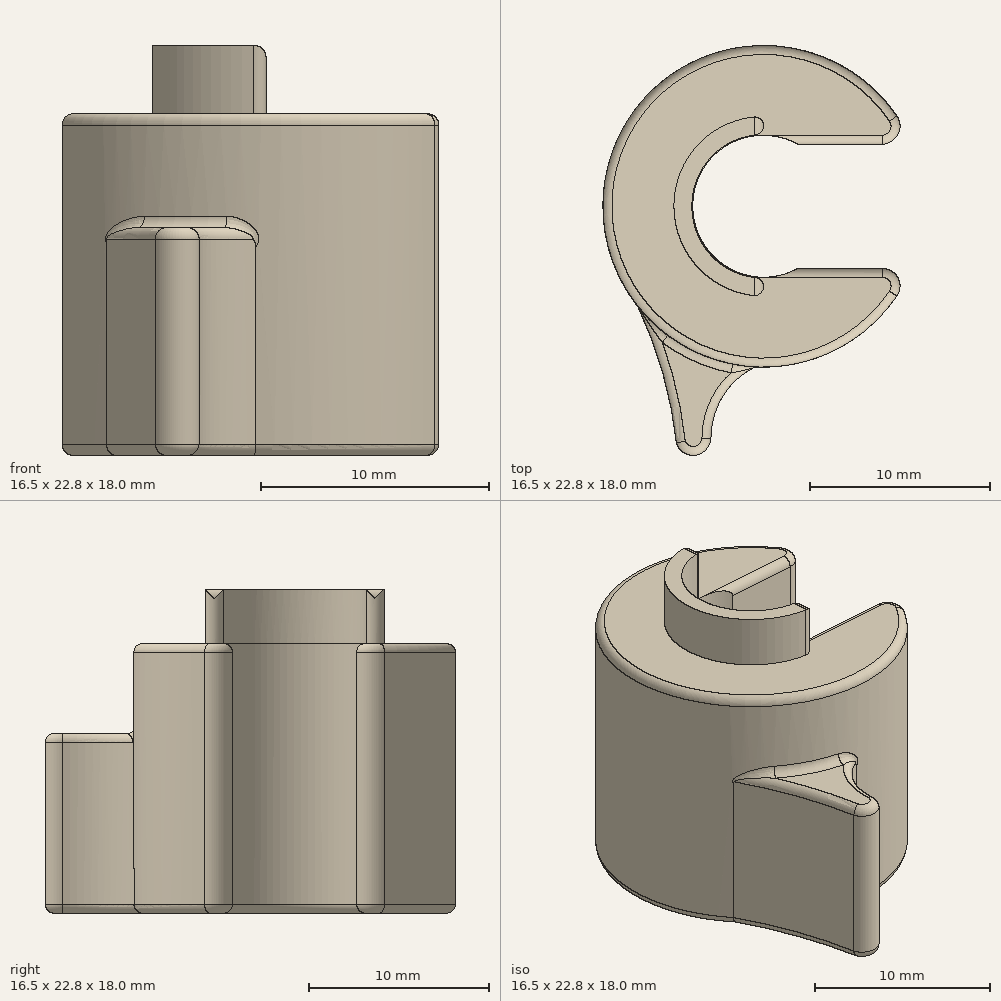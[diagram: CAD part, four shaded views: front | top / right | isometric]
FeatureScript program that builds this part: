
annotation { "Feature Type Name" : "Feature", "Feature Type Description" : "" }
export const myFeature = defineFeature(function(context is Context, id is Id, definition is map)
    precondition{}
    {
        {
            var Q0;
            Q0=qCreatedBy(makeId("Top.planeOp"),FACE);
            var sketch = newSketch(context, id + "F0", { "sketchPlane" : qUnion([Q0])});
            skCircle(sketch, "E0", {"center": v(0, 0) * mm, "radius": 3.95 * mm});
            skCircle(sketch, "E1", {"center": v(0, 0) * mm, "radius": 8.95 * mm});
            skLineSegment(sketch, "E2", {"start": v(0, 3.45) * mm, "end": v(8.26, 3.45) * mm});
            skLineSegment(sketch, "E3", {"start": v(0, -3.45) * mm, "end": v(8.26, -3.45) * mm});
            skLineSegment(sketch, "E4", {"start": v(0, 3.45) * mm, "end": v(0, -3.45) * mm});
            skSolve(sketch);
        }
        {
            var Q0;
            {var subQ0=sQuery(id+"F0.wireOp",EDGE,"E2");var subQ1=sQuery(id+"F0.wireOp",EDGE,"E0");var subQ2=makeQuery(id+"F0.imprint","INTERSECT",VERTEX,{"derivedFrom":[subQ1,subQ0]});Q0=makeQuery(id+"F0.imprint","IMPRINT",FACE,{"disambiguationData":[TD([[makeQuery(id+"F0.imprint","IMPRINT",EDGE,{"disambiguationData":[TD([[subQ2,-1.0]])],"derivedFrom":subQ1}),-1.0]])]});}
            extrude(context, id + "F1", {"entities" : qUnion([Q0]), "depth" : 15 * mm, "offsetDistance" : 25 * mm});
        }
        {
            var Q0;
            Q0=makeQuery(id+"F1.opExtrude","SWEPT_EDGE",EDGE,{"disambiguationData":[OSD([sQuery(id+"F0.wireOp",EDGE,"E1"),sQuery(id+"F0.wireOp",EDGE,"E2")])]});
            var Q1;
            Q1=makeQuery(id+"F1.opExtrude","SWEPT_EDGE",EDGE,{"disambiguationData":[OSD([sQuery(id+"F0.wireOp",EDGE,"E1"),sQuery(id+"F0.wireOp",EDGE,"E3")])]});
            fillet(context, id + "F2", {"entities" : qUnion([Q0, Q1]), "radius" : 1 * mm, "tangentPropagation" : true, "allowEdgeOverflow" : false});
        }
        {
            var Q0;
            Q0=makeQuery(id+"F1.opExtrude","CAP_FACE",FACE,{"disambiguationData":[OSD([sQuery(id+"F0.wireOp",EDGE,"E0"),sQuery(id+"F0.wireOp",EDGE,"E1"),sQuery(id+"F0.wireOp",EDGE,"E2"),sQuery(id+"F0.wireOp",EDGE,"E3")])],"isStart":false});
            var sketch = newSketch(context, id + "F3", { "sketchPlane" : qUnion([Q0])});
            skCircle(sketch, "E5", {"center": v(0, 0) * mm, "radius": 4 * mm});
            skCircle(sketch, "E6", {"center": v(0, 0) * mm, "radius": 5 * mm});
            skLineSegment(sketch, "E7", {"start": v(0, 5) * mm, "end": v(0, -5) * mm});
            skSolve(sketch);
        }
        {
            var Q0;
            {var subQ0=sQuery(id+"F3.wireOp",EDGE,"E7");var subQ1=sQuery(id+"F3.wireOp",EDGE,"E5");var subQ2=makeQuery(id+"F3.imprint","INTERSECT",VERTEX,{"disambiguationData":[OD(0.0)],"derivedFrom":[subQ1,subQ0]});Q0=makeQuery(id+"F3.imprint","IMPRINT",FACE,{"disambiguationData":[TD([[makeQuery(id+"F3.imprint","IMPRINT",EDGE,{"disambiguationData":[TD([[subQ2,-1.0]])],"derivedFrom":subQ1}),-1.0]])]});}
            extrude(context, id + "F4", {"entities" : qUnion([Q0]), "operationType" : NewBodyOperationType.ADD, "depth" : 3 * mm, "offsetDistance" : 25 * mm});
        }
        {
            var Q0;
            Q0=makeQuery(id+"F1.opExtrude","CAP_FACE",FACE,{"disambiguationData":[OSD([sQuery(id+"F0.wireOp",EDGE,"E0"),sQuery(id+"F0.wireOp",EDGE,"E1"),sQuery(id+"F0.wireOp",EDGE,"E2"),sQuery(id+"F0.wireOp",EDGE,"E3")])],"isStart":true});
            var sketch = newSketch(context, id + "F5", { "sketchPlane" : qUnion([Q0])});
            skArc(sketch, "E8", {"start": v(-2.94, 12.9) * mm, "mid": v(-1.26, 9.46) * mm, "end": v(2.47, 8.6) * mm});
            skArc(sketch, "E9", {"start": v(-2.94, 12.9) * mm, "mid": v(-3.78, 13.86) * mm, "end": v(-4.86, 13.17) * mm});
            skArc(sketch, "E10", {"start": v(-7, 5.57) * mm, "mid": v(-5.62, 9.28) * mm, "end": v(-4.86, 13.17) * mm});
            skArc(sketch, "E11.MirrorCS", {"start": v(-7, -5.57) * mm, "mid": v(-5.62, -9.28) * mm, "end": v(-4.86, -13.17) * mm});
            skArc(sketch, "E12.MirrorCS", {"start": v(-2.94, -12.9) * mm, "mid": v(-1.26, -9.46) * mm, "end": v(2.47, -8.6) * mm});
            skArc(sketch, "E13.MirrorCS", {"start": v(-2.94, -12.9) * mm, "mid": v(-3.78, -13.86) * mm, "end": v(-4.86, -13.17) * mm});
            skSolve(sketch);
        }
        {
            var Q0;
            {var subQ0=sQuery(id+"F5.wireOp",EDGE,"E9");Q0=makeQuery(id+"F5.imprint","IMPRINT",FACE,{"disambiguationData":[TD([[makeQuery(id+"F5.imprint","IMPRINT",EDGE,{"derivedFrom":subQ0}),1.0]])]});}
            var Q1;
            {var subQ0=sQuery(id+"F5.wireOp",EDGE,"E11.MirrorCS");Q1=makeQuery(id+"F5.imprint","IMPRINT",FACE,{"disambiguationData":[TD([[makeQuery(id+"F5.imprint","IMPRINT",EDGE,{"derivedFrom":subQ0}),1.0]])]});}
            extrude(context, id + "F6", {"entities" : qUnion([Q0, Q1]), "operationType" : NewBodyOperationType.ADD, "oppositeDirection" : true, "depth" : 10 * mm, "offsetDistance" : 25 * mm});
        }
        {
            var Q0;
            {var subQ0=sQuery(id+"F3.wireOp",EDGE,"E7");var subQ1=sQuery(id+"F3.wireOp",EDGE,"E5");Q0=makeQuery(id+"F4.opExtrude","SWEPT_EDGE",EDGE,{"disambiguationData":[OSD([subQ1,subQ0]),TDD([makeQuery(id+"F3.imprint","INTERSECT",VERTEX,{"disambiguationData":[OD(0.0)],"derivedFrom":[subQ1,subQ0]})])]});}
            var Q1;
            {var subQ0=sQuery(id+"F3.wireOp",EDGE,"E7");Q1=makeQuery(id+"F4.opExtrude","CAP_EDGE",EDGE,{"disambiguationData":[OSD([subQ0]),TDD([makeQuery(id+"F3.imprint","IMPRINT",EDGE,{"disambiguationData":[TD([[makeQuery(id+"F3.imprint","INTERSECT",VERTEX,{"disambiguationData":[OD(1.0)],"derivedFrom":[sQuery(id+"F3.wireOp",EDGE,"E6"),subQ0]}),1.0]])],"derivedFrom":subQ0})])],"isStart":false});}
            var Q2;
            {var subQ0=sQuery(id+"F3.wireOp",EDGE,"E7");var subQ1=sQuery(id+"F3.wireOp",EDGE,"E5");Q2=makeQuery(id+"F4.opExtrude","SWEPT_EDGE",EDGE,{"disambiguationData":[OSD([subQ1,subQ0]),TDD([makeQuery(id+"F3.imprint","INTERSECT",VERTEX,{"disambiguationData":[OD(1.0)],"derivedFrom":[subQ1,subQ0]})])]});}
            var Q3;
            {var subQ0=sQuery(id+"F3.wireOp",EDGE,"E7");Q3=makeQuery(id+"F4.opExtrude","CAP_EDGE",EDGE,{"disambiguationData":[OSD([subQ0]),TDD([makeQuery(id+"F3.imprint","IMPRINT",EDGE,{"disambiguationData":[TD([[makeQuery(id+"F3.imprint","INTERSECT",VERTEX,{"disambiguationData":[OD(0.0)],"derivedFrom":[sQuery(id+"F3.wireOp",EDGE,"E6"),subQ0]}),-1.0]])],"derivedFrom":subQ0})])],"isStart":false});}
            var Q4;
            {var subQ0=sQuery(id+"F3.wireOp",EDGE,"E7");var subQ1=sQuery(id+"F3.wireOp",EDGE,"E6");Q4=makeQuery(id+"F4.opExtrude","SWEPT_EDGE",EDGE,{"disambiguationData":[OSD([subQ1,subQ0]),TDD([makeQuery(id+"F3.imprint","INTERSECT",VERTEX,{"disambiguationData":[OD(1.0)],"derivedFrom":[subQ1,subQ0]})])]});}
            var Q5;
            {var subQ0=sQuery(id+"F3.wireOp",EDGE,"E7");var subQ1=sQuery(id+"F3.wireOp",EDGE,"E6");Q5=makeQuery(id+"F4.opExtrude","SWEPT_EDGE",EDGE,{"disambiguationData":[OSD([subQ1,subQ0]),TDD([makeQuery(id+"F3.imprint","INTERSECT",VERTEX,{"disambiguationData":[OD(0.0)],"derivedFrom":[subQ1,subQ0]})])]});}
            var Q6;
            Q6=makeQuery(id+"F1.opExtrude","CAP_EDGE",EDGE,{"disambiguationData":[OSD([sQuery(id+"F0.wireOp",EDGE,"E3")])],"isStart":false});
            var Q7;
            Q7=makeQuery(id+"F1.opExtrude","CAP_EDGE",EDGE,{"disambiguationData":[OSD([sQuery(id+"F0.wireOp",EDGE,"E0")])],"isStart":true});
            var Q8;
            {var subQ0=sQuery(id+"F0.wireOp",EDGE,"E2");var subQ1=sQuery(id+"F0.wireOp",EDGE,"E1");Q8=makeQuery(id+"F2.opFillet","BLEND_EDGE",EDGE,{"blendedFrom":[makeQuery(id+"F1.opExtrude","SWEPT_EDGE",EDGE,{"disambiguationData":[OSD([subQ1,subQ0])]}),makeQuery(id+"F1.opExtrude","CAP_FACE",FACE,{"disambiguationData":[OSD([sQuery(id+"F0.wireOp",EDGE,"E0"),subQ1,subQ0,sQuery(id+"F0.wireOp",EDGE,"E3")])],"isStart":true})],"blendedInto":[makeQuery(id+"F1.opExtrude","CAP_FACE",FACE,{"disambiguationData":[OSD([sQuery(id+"F0.wireOp",EDGE,"E0"),subQ1,subQ0,sQuery(id+"F0.wireOp",EDGE,"E3")])],"isStart":true})]});}
            var Q9;
            {var subQ0=sQuery(id+"F0.wireOp",EDGE,"E1");Q9=makeQuery(id+"F6.boolean.opBoolean","MERGE",FACE,{"derivedFrom":[makeQuery(id+"F1.opExtrude","CAP_FACE",FACE,{"disambiguationData":[OSD([sQuery(id+"F0.wireOp",EDGE,"E0"),subQ0,sQuery(id+"F0.wireOp",EDGE,"E2"),sQuery(id+"F0.wireOp",EDGE,"E3")])],"isStart":true}),makeQuery(id+"F6.opExtrude","CAP_FACE",FACE,{"disambiguationData":[OSD([subQ0,sQuery(id+"F5.wireOp",EDGE,"E8"),sQuery(id+"F5.wireOp",EDGE,"E9"),sQuery(id+"F5.wireOp",EDGE,"E10")])],"isStart":true}),makeQuery(id+"F6.opExtrude","CAP_FACE",FACE,{"disambiguationData":[OSD([subQ0,sQuery(id+"F5.wireOp",EDGE,"E11.MirrorCS"),sQuery(id+"F5.wireOp",EDGE,"E12.MirrorCS"),sQuery(id+"F5.wireOp",EDGE,"E13.MirrorCS")])],"isStart":true})]});}
            var Q10;
            Q10=makeQuery(id+"F6.opExtrude","CAP_FACE",FACE,{"disambiguationData":[OSD([sQuery(id+"F0.wireOp",EDGE,"E1"),sQuery(id+"F5.wireOp",EDGE,"E11.MirrorCS"),sQuery(id+"F5.wireOp",EDGE,"E12.MirrorCS"),sQuery(id+"F5.wireOp",EDGE,"E13.MirrorCS")])],"isStart":false});
            var Q11;
            Q11=makeQuery(id+"F6.opExtrude","CAP_FACE",FACE,{"disambiguationData":[OSD([sQuery(id+"F0.wireOp",EDGE,"E1"),sQuery(id+"F5.wireOp",EDGE,"E8"),sQuery(id+"F5.wireOp",EDGE,"E9"),sQuery(id+"F5.wireOp",EDGE,"E10")])],"isStart":false});
            fillet(context, id + "F7", {"entities" : qUnion([Q0, Q1, Q2, Q3, Q4, Q5, Q6, Q7, Q8, Q9, Q10, Q11]), "radius" : 0.5 * mm, "tangentPropagation" : true, "allowEdgeOverflow" : false});
        }
    });
